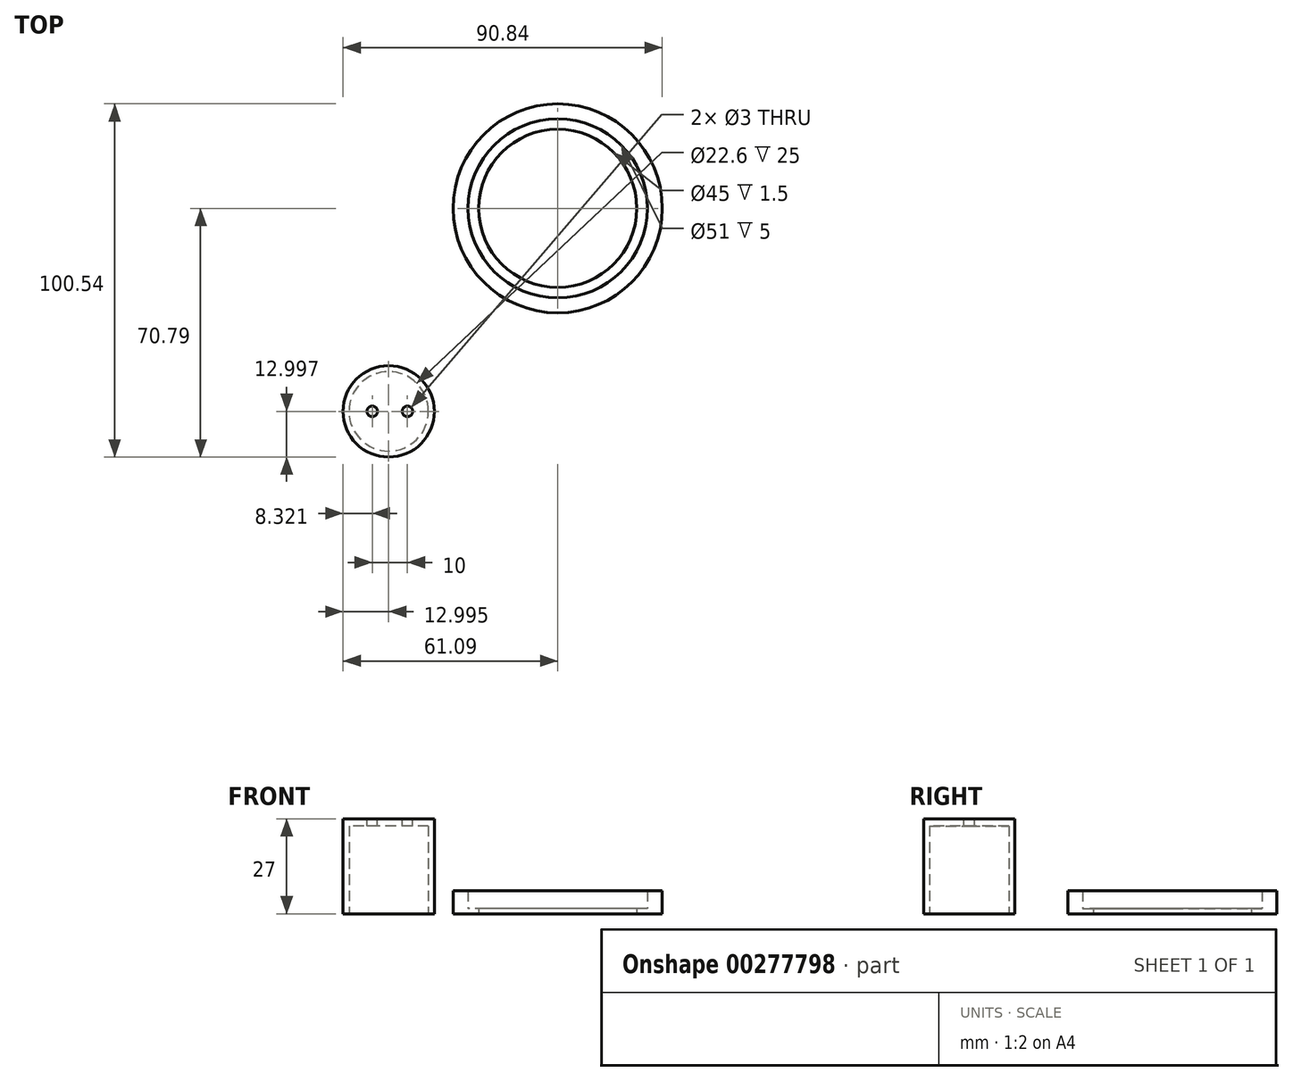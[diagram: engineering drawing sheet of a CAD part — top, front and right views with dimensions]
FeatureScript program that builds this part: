
annotation { "Feature Type Name" : "Feature", "Feature Type Description" : "" }
export const myFeature = defineFeature(function(context is Context, id is Id, definition is map)
    precondition{}
    {
        {
            var Q0;
            Q0=qCreatedBy(makeId("Top.planeOp"),FACE);
            var sketch = newSketch(context, id + "F0", { "sketchPlane" : qUnion([Q0])});
            skCircle(sketch, "E0", {"center": v(0, 0) * mm, "radius": 29.75 * mm});
            skCircle(sketch, "E1", {"center": v(0, 0) * mm, "radius": 22.5 * mm});
            skSolve(sketch);
        }
        {
            var Q0;
            Q0=makeQuery(id+"F0.imprint","IMPRINT",FACE,{"disambiguationData":[TD([[makeQuery(id+"F0.imprint","IMPRINT",EDGE,{"derivedFrom":sQuery(id+"F0.wireOp",EDGE,"E0")}),1.0]])]});
            extrude(context, id + "F1", {"entities" : qUnion([Q0]), "depth" : 1.5 * mm});
        }
        {
            var Q0;
            Q0=makeQuery(id+"F1.opExtrude","CAP_FACE",FACE,{"disambiguationData":[OSD([sQuery(id+"F0.wireOp",EDGE,"E0"),sQuery(id+"F0.wireOp",EDGE,"E1")])],"isStart":false});
            var sketch = newSketch(context, id + "F2", { "sketchPlane" : qUnion([Q0])});
            skCircle(sketch, "E2", {"center": v(0, 0) * mm, "radius": 29.75 * mm});
            skPoint(sketch, "E2.first.point", {"position": v(-12.06, 27.2) * mm});
            skPoint(sketch, "E2.second.point", {"position": v(0, -29.75) * mm});
            skPoint(sketch, "E2.third.point", {"position": v(24.47, -16.92) * mm});
            skCircle(sketch, "E3", {"center": v(0, 0) * mm, "radius": 25.5 * mm});
            skSolve(sketch);
        }
        {
            var Q0;
            Q0=makeQuery(id+"F2.imprint","IMPRINT",FACE,{"disambiguationData":[TD([[makeQuery(id+"F2.imprint","IMPRINT",EDGE,{"derivedFrom":sQuery(id+"F2.wireOp",EDGE,"E2")}),1.0]])]});
            extrude(context, id + "F3", {"entities" : qUnion([Q0]), "operationType" : NewBodyOperationType.ADD, "depth" : 5 * mm});
        }
        {
            var Q0;
            Q0=qCreatedBy(makeId("Top.planeOp"),FACE);
            var sketch = newSketch(context, id + "F4", { "sketchPlane" : qUnion([Q0])});
            skCircle(sketch, "E4", {"center": v(-48.1, -57.8) * mm, "radius": 11.3 * mm});
            skCircle(sketch, "E5", {"center": v(-48.1, -57.8) * mm, "radius": 13 * mm});
            skSolve(sketch);
        }
        {
            var Q0;
            Q0=makeQuery(id+"F4.imprint","IMPRINT",FACE,{"disambiguationData":[TD([[makeQuery(id+"F4.imprint","IMPRINT",EDGE,{"derivedFrom":sQuery(id+"F4.wireOp",EDGE,"E4")}),-1.0]])]});
            extrude(context, id + "F5", {"entities" : qUnion([Q0]), "depth" : 25 * mm});
        }
        {
            var Q0;
            Q0=makeQuery(id+"F5.opExtrude","CAP_FACE",FACE,{"disambiguationData":[OSD([sQuery(id+"F4.wireOp",EDGE,"E4"),sQuery(id+"F4.wireOp",EDGE,"E5")])],"isStart":false});
            var sketch = newSketch(context, id + "F6", { "sketchPlane" : qUnion([Q0])});
            skCircle(sketch, "E6", {"center": v(-48.1, -57.8) * mm, "radius": 13 * mm});
            skPoint(sketch, "E6.first.point", {"position": v(-60.2, -53.06) * mm});
            skPoint(sketch, "E6.second.point", {"position": v(-40.68, -47.11) * mm});
            skPoint(sketch, "E6.third.point", {"position": v(-43.5, -69.95) * mm});
            skSolve(sketch);
        }
        {
            var Q0;
            Q0 = qSketchRegion(id + "F6", true);
            extrude(context, id + "F7", {"entities" : qUnion([Q0]), "operationType" : NewBodyOperationType.ADD, "depth" : 2 * mm});
        }
        {
            var Q0;
            Q0=makeQuery(id+"F7.opExtrude","CAP_FACE",FACE,{"disambiguationData":[OSD([sQuery(id+"F6.wireOp",EDGE,"E6")])],"isStart":false});
            var sketch = newSketch(context, id + "F8", { "sketchPlane" : qUnion([Q0])});
            skLineSegment(sketch, "E7", {"start": v(-48.1, -57.8) * mm, "end": v(-61.1, -57.8) * mm, "construction": true});
            skLineSegment(sketch, "E8", {"start": v(-48.1, -57.8) * mm, "end": v(-35.1, -57.8) * mm, "construction": true});
            skCircle(sketch, "E9", {"center": v(-52.77, -57.8) * mm, "radius": 1.5 * mm});
            skCircle(sketch, "E10", {"center": v(-42.77, -57.8) * mm, "radius": 1.5 * mm});
            skSolve(sketch);
        }
        {
            var Q0;
            Q0=makeQuery(id+"F8.imprint","IMPRINT",FACE,{"disambiguationData":[TD([[makeQuery(id+"F8.imprint","IMPRINT",EDGE,{"derivedFrom":sQuery(id+"F8.wireOp",EDGE,"E10")}),1.0]])]});
            var Q1;
            Q1=makeQuery(id+"F8.imprint","IMPRINT",FACE,{"disambiguationData":[TD([[makeQuery(id+"F8.imprint","IMPRINT",EDGE,{"derivedFrom":sQuery(id+"F8.wireOp",EDGE,"E9")}),1.0]])]});
            extrude(context, id + "F9", {"entities" : qUnion([Q0, Q1]), "operationType" : NewBodyOperationType.REMOVE, "endBound" : BoundingType.UP_TO_NEXT, "oppositeDirection" : true, "depth" : 25 * mm});
        }
    });
